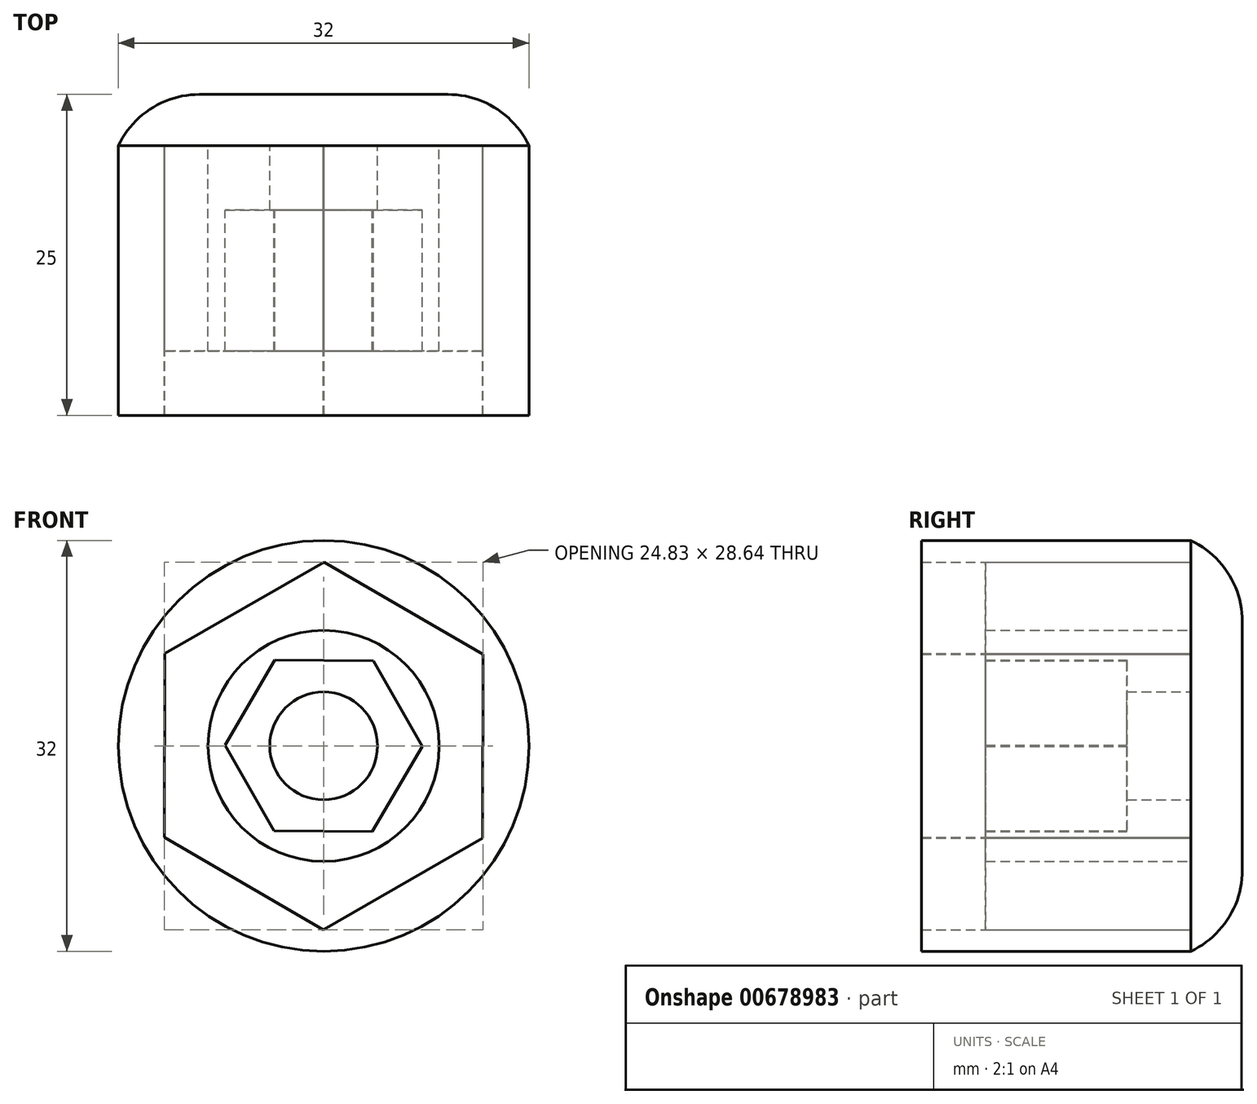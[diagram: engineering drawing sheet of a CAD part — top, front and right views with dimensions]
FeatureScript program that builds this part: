
annotation { "Feature Type Name" : "Feature", "Feature Type Description" : "" }
export const myFeature = defineFeature(function(context is Context, id is Id, definition is map)
    precondition{}
    {
        {
            var Q0;
            Q0=qCreatedBy(makeId("Front.planeOp"),FACE);
            var sketch = newSketch(context, id + "F0", { "sketchPlane" : qUnion([Q0])});
            skCircle(sketch, "E0", {"center": v(0, 0) * mm, "radius": 16 * mm});
            skCircle(sketch, "E1.cCircle", {"center": v(0, 0) * mm, "radius": 12.4 * mm, "construction": true});
            skLineSegment(sketch, "E1.0", {"start": v(-12.38, 7.19) * mm, "end": v(0.03, 14.32) * mm});
            skLineSegment(sketch, "E1.1", {"start": v(0.03, 14.32) * mm, "end": v(12.42, 7.13) * mm});
            skLineSegment(sketch, "E1.2", {"start": v(12.42, 7.13) * mm, "end": v(12.38, -7.19) * mm});
            skLineSegment(sketch, "E1.3", {"start": v(12.38, -7.19) * mm, "end": v(-0.03, -14.32) * mm});
            skLineSegment(sketch, "E1.4", {"start": v(-0.03, -14.32) * mm, "end": v(-12.42, -7.13) * mm});
            skLineSegment(sketch, "E1.5", {"start": v(-12.42, -7.13) * mm, "end": v(-12.38, 7.19) * mm});
            skPoint(sketch, "E1.0.midPoint", {"position": v(-6.17, 10.75) * mm});
            skCircle(sketch, "E2", {"center": v(0, 0) * mm, "radius": 9 * mm});
            skCircle(sketch, "E3.cCircle", {"center": v(0, 0) * mm, "radius": 6.65 * mm, "construction": true});
            skLineSegment(sketch, "E3.0", {"start": v(-7.68, 0.05) * mm, "end": v(-3.8, 6.68) * mm});
            skLineSegment(sketch, "E3.1", {"start": v(-3.8, 6.68) * mm, "end": v(3.88, 6.62) * mm});
            skLineSegment(sketch, "E3.2", {"start": v(3.88, 6.62) * mm, "end": v(7.68, -0.05) * mm});
            skLineSegment(sketch, "E3.3", {"start": v(7.68, -0.05) * mm, "end": v(3.8, -6.68) * mm});
            skLineSegment(sketch, "E3.4", {"start": v(3.8, -6.68) * mm, "end": v(-3.88, -6.62) * mm});
            skLineSegment(sketch, "E3.5", {"start": v(-3.88, -6.62) * mm, "end": v(-7.68, 0.05) * mm});
            skPoint(sketch, "E3.0.midPoint", {"position": v(-5.74, 3.36) * mm});
            skCircle(sketch, "E4", {"center": v(0, 0) * mm, "radius": 4.2 * mm});
            skSolve(sketch);
        }
        {
            var Q0;
            Q0=makeQuery(id+"F0.imprint","IMPRINT",FACE,{"disambiguationData":[TD([[makeQuery(id+"F0.imprint","IMPRINT",EDGE,{"derivedFrom":sQuery(id+"F0.wireOp",EDGE,"E0")}),1.0]])]});
            extrude(context, id + "F1", {"entities" : qUnion([Q0]), "depth" : 21 * mm, "offsetDistance" : 25 * mm});
        }
        {
            var Q0;
            Q0=makeQuery(id+"F0.imprint","IMPRINT",FACE,{"disambiguationData":[TD([[makeQuery(id+"F0.imprint","IMPRINT",EDGE,{"derivedFrom":sQuery(id+"F0.wireOp",EDGE,"E2")}),1.0]])]});
            extrude(context, id + "F2", {"entities" : qUnion([Q0]), "depth" : 16 * mm, "offsetDistance" : 25 * mm});
        }
        {
            var Q0;
            Q0=qCreatedBy(makeId("Front.planeOp"),FACE);
            var sketch = newSketch(context, id + "F3", { "sketchPlane" : qUnion([Q0])});
            skCircle(sketch, "E5", {"center": v(0, 0) * mm, "radius": 16 * mm});
            skSolve(sketch);
        }
        {
            var Q0;
            Q0 = qSketchRegion(id + "F3", true);
            extrude(context, id + "F4", {"entities" : qUnion([Q0]), "depth" : -4 * mm, "offsetDistance" : 25 * mm});
        }
        {
            var Q0;
            Q0=makeQuery(id+"F0.imprint","IMPRINT",FACE,{"disambiguationData":[TD([[makeQuery(id+"F0.imprint","IMPRINT",EDGE,{"derivedFrom":sQuery(id+"F0.wireOp",EDGE,"E1.0")}),-1.0]])]});
            extrude(context, id + "F5", {"entities" : qUnion([Q0]), "depth" : 16 * mm, "offsetDistance" : 25 * mm});
        }
        {
            var Q0;
            Q0=makeQuery(id+"F4.opExtrude","CAP_FACE",FACE,{"disambiguationData":[OSD([sQuery(id+"F3.wireOp",EDGE,"E5")])],"isStart":false});
            fillet(context, id + "F6", {"entities" : qUnion([Q0]), "radius" : 7 * mm, "tangentPropagation" : true, "allowEdgeOverflow" : false});
        }
        {
            var Q0;
            Q0=makeQuery(id+"F0.imprint","IMPRINT",FACE,{"disambiguationData":[TD([[makeQuery(id+"F0.imprint","IMPRINT",EDGE,{"derivedFrom":sQuery(id+"F0.wireOp",EDGE,"E3.0")}),-1.0]])]});
            extrude(context, id + "F7", {"entities" : qUnion([Q0]), "operationType" : NewBodyOperationType.ADD, "depth" : 5 * mm, "offsetDistance" : 25 * mm});
        }
    });
